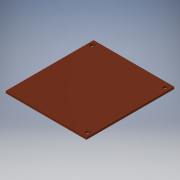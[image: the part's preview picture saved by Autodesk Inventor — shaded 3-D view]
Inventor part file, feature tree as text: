
AUTODESK INVENTOR PART (.ipt)
format: ipt  version: 2019 (Build 230136000, 136)  size: 109,568 bytes
history: native  units: mm
features: plane x2, sketch x2, extrude x1, hole x1
ambient origin geometry x8: Origin, YZ Plane, XZ Plane, XY Plane, X Axis, Y Axis, Z Axis, Center Point
bodies: Solid1 (feature_tree)
feature tree (6):
  extrude  "Extrusion1"  Depth=77.47mm
  hole  "Hole1"  [1 undecoded]
  plane  "Work Plane1"
  plane  "Work Plane2"
  sketch  "Sketch1"  dims[d0=71.12mm d1=77.47mm]
  sketch  "Sketch2"  dims[d2=1.6mm d3=0.0mm d4=68.58mm d5=64.516mm d6=3.4mm d7=6.0mm d8=6.3mm d9=2.0mm d10=90.0deg d11=8.0mm d12=20.594885mm]
note: 1 required parameter value undecoded (feature->parameter linkage not recoverable at this tier; creation-order binding heuristic only, values carry confidence <= 0.55)
